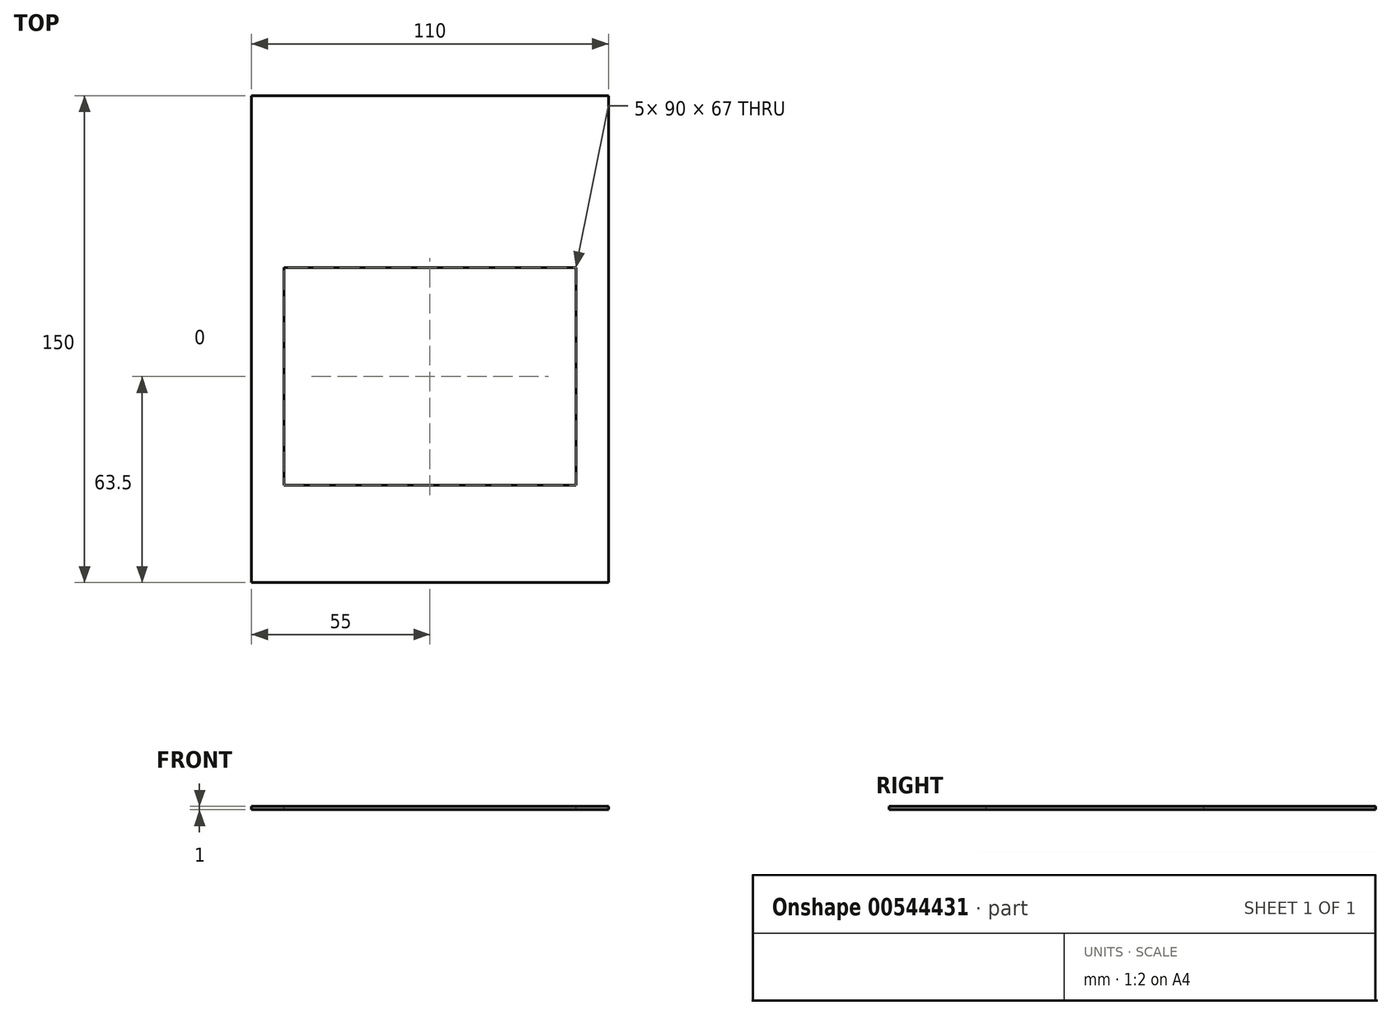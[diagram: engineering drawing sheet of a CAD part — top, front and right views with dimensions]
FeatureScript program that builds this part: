
annotation { "Feature Type Name" : "Feature", "Feature Type Description" : "" }
export const myFeature = defineFeature(function(context is Context, id is Id, definition is map)
    precondition{}
    {
        {
            var Q0;
            Q0=qCreatedBy(makeId("Top.planeOp"),FACE);
            var sketch = newSketch(context, id + "F0", { "sketchPlane" : qUnion([Q0])});
            skLineSegment(sketch, "E0.bottom", {"start": v(-55, -75) * mm, "end": v(55, -75) * mm});
            skLineSegment(sketch, "E0.top", {"start": v(-55, 75) * mm, "end": v(55, 75) * mm});
            skLineSegment(sketch, "E0.left", {"start": v(-55, -75) * mm, "end": v(-55, 75) * mm});
            skLineSegment(sketch, "E0.right", {"start": v(55, -75) * mm, "end": v(55, 75) * mm});
            skPoint(sketch, "E0.middle", {"position": v(0, 0) * mm});
            skSolve(sketch);
        }
        {
            var Q0;
            Q0 = qSketchRegion(id + "F0", true);
            extrude(context, id + "F1", {"entities" : qUnion([Q0]), "depth" : 1 * mm, "offsetDistance" : 25 * mm});
        }
        {
            var Q0;
            Q0=makeQuery(id+"F1.opExtrude","CAP_FACE",FACE,{"disambiguationData":[OSD([sQuery(id+"F0.wireOp",EDGE,"E0.bottom"),sQuery(id+"F0.wireOp",EDGE,"E0.top"),sQuery(id+"F0.wireOp",EDGE,"E0.left"),sQuery(id+"F0.wireOp",EDGE,"E0.right")])],"isStart":false});
            var sketch = newSketch(context, id + "F2", { "sketchPlane" : qUnion([Q0])});
            skLineSegment(sketch, "E1.bottom", {"start": v(45, 22) * mm, "end": v(-45, 22) * mm});
            skLineSegment(sketch, "E1.top", {"start": v(45, -45) * mm, "end": v(-45, -45) * mm});
            skLineSegment(sketch, "E1.left", {"start": v(45, 22) * mm, "end": v(45, -45) * mm});
            skLineSegment(sketch, "E1.right", {"start": v(-45, 22) * mm, "end": v(-45, -45) * mm});
            skSolve(sketch);
        }
        {
            var Q0;
            Q0=makeQuery(id+"F2.imprint","IMPRINT",FACE,{"disambiguationData":[TD([[makeQuery(id+"F2.imprint","IMPRINT",EDGE,{"derivedFrom":sQuery(id+"F2.wireOp",EDGE,"E1.bottom")}),1.0]])]});
            extrude(context, id + "F3", {"entities" : qUnion([Q0]), "operationType" : NewBodyOperationType.REMOVE, "oppositeDirection" : true, "depth" : 25 * mm, "offsetDistance" : 25 * mm});
        }
    });
